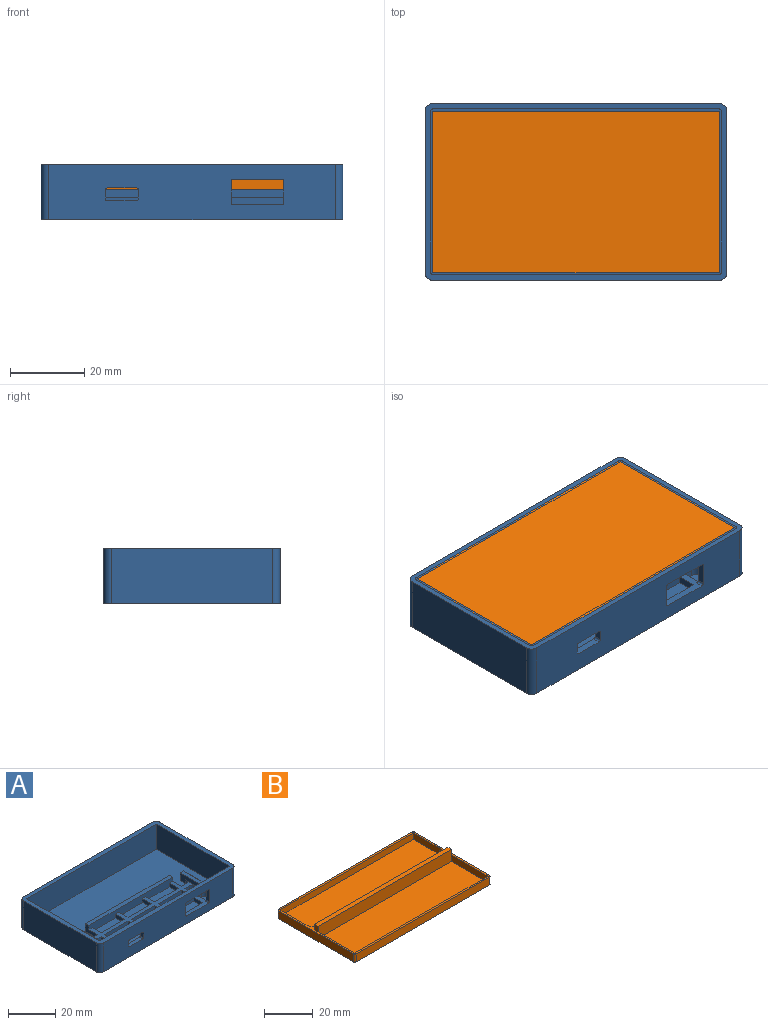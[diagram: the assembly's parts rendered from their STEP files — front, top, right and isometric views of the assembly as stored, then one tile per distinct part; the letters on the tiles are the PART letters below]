
ASSEMBLY  parts=2 mates=1
PART A: 116 faces, bbox 81.4x47.6x15 mm
  f0: plane 5.4x4.6mm, normal (0,0,1), area 24mm2, adj f10,f36,f56,f83,f110
  f1: plane 5.4x4.6mm, normal (0,0,1), area 23.1mm2, adj f36,f53,f55,f80,f85,f112
  f2: plane 50x4mm, normal (0,-1,0), area 184mm2, adj f11,f18,f25,f54,f88,f89,f90,f96
  f3: plane 77.4x43.6mm, normal (0,0,1), area 1884.4mm2, adj f10,f26,f30,f31,f36,f37,f38,f49
  f4: plane 14x2mm, normal (0,1,0), area 28mm2, adj f11,f54,f107,f113
  f5: plane 14x2mm, normal (0,-1,0), area 28mm2, adj f9,f54,f106,f111
  f6: plane 14x2mm, normal (0,1,0), area 28mm2, adj f9,f54,f106,f111
  f7: plane 14x2mm, normal (0,-1,0), area 28mm2, adj f8,f54,f104,f109
  f8: plane 14x5.4mm, normal (0,0,1), area 75.6mm2, adj f7,f10,f104,f109
  f9: plane 14x5.4mm, normal (0,0,1), area 75.6mm2, adj f5,f6,f106,f111
  f10: plane 77.4x13mm, normal (0,1,0), area 722mm2, adj f0,f3,f8,f23,f32,f35,f36,f37
  f11: plane 14x5.4mm, normal (0,0,1), area 75.6mm2, adj f2,f4,f107,f113
  f12: plane 14x2mm, normal (0,1,0), area 28mm2, adj f18,f54,f98,f108
  f13: plane 14x2mm, normal (0,-1,0), area 28mm2, adj f17,f54,f101,f105
  f14: plane 14x2mm, normal (0,1,0), area 28mm2, adj f17,f54,f101,f105
  f15: plane 14x2mm, normal (0,-1,0), area 28mm2, adj f16,f54,f100,f103
  f16: plane 14x5.4mm, normal (0,0,1), area 75.6mm2, adj f15,f33,f100,f103
  f17: plane 14x5.4mm, normal (0,0,1), area 75.6mm2, adj f13,f14,f101,f105
  f18: plane 14x5.4mm, normal (0,0,1), area 75.6mm2, adj f2,f12,f98,f108
  f19: plane 14x2mm, normal (0,1,0), area 28mm2, adj f25,f54,f96,f97
  f20: plane 14x2mm, normal (0,-1,0), area 28mm2, adj f24,f54,f94,f102
  f21: plane 14x2mm, normal (0,1,0), area 28mm2, adj f24,f54,f94,f102
  f22: plane 14x2mm, normal (0,-1,0), area 28mm2, adj f23,f54,f93,f99
  f23: plane 14x5.4mm, normal (0,0,1), area 75.6mm2, adj f10,f22,f93,f99
  f24: plane 14x5.4mm, normal (0,0,1), area 75.6mm2, adj f20,f21,f94,f102
  f25: plane 14x5.4mm, normal (0,0,1), area 75.6mm2, adj f2,f19,f96,f97
  f26: plane 2.6x2mm, normal (0,1,0), area 5.2mm2, adj f3,f54,f87,f90
  f27: plane 2.6x2mm, normal (0,-1,0), area 5.2mm2, adj f39,f54,f86,f95
  f28: plane 2.6x2mm, normal (0,1,0), area 5.2mm2, adj f39,f54,f81,f95
  f29: plane 2.6x2mm, normal (0,-1,0), area 5.2mm2, adj f35,f54,f82,f92
  f30: plane 6x4mm, normal (0,1,0), area 16mm2, adj f3,f50,f51,f115
  f31: plane 6x4mm, normal (0,1,0), area 16mm2, adj f3,f32,f36,f114
  f32: plane 20.2x2mm, normal (0,0,1), area 40.4mm2, adj f10,f31,f36,f114
  f33: plane 14x2mm, normal (0,1,0), area 28mm2, adj f16,f54,f100,f103
  f34: plane 77.4x15mm, normal (0,-1,0), area 1031.9mm2, adj f40,f44,f45,f48,f54,f57,f58,f59
  f35: plane 5.4x4.6mm, normal (0,0,1), area 24mm2, adj f10,f29,f50,f82,f92
  f36: plane 20.2x4mm, normal (-1,0,0), area 56.8mm2, adj f0,f1,f3,f10,f31,f32,f54,f80
  f37: plane 43.6x13mm, normal (-1,0,0), area 566.8mm2, adj f3,f10,f40,f49
  f38: plane 43.6x13mm, normal (1,0,0), area 566.8mm2, adj f3,f10,f40,f49
  f39: plane 5.4x4.6mm, normal (0,0,1), area 23.1mm2, adj f27,f28,f50,f81,f86,f95
  f40: plane 81.4x47.6mm, normal (0,0,1), area 496.6mm2, adj f10,f34,f37,f38,f41,f42,f43,f45
  f41: plane 43.6x15mm, normal (1,0,0), area 654mm2, adj f40,f44,f45,f46
  f42: plane 77.4x15mm, normal (0,1,0), area 1161mm2, adj f40,f44,f46,f47
  f43: plane 43.6x15mm, normal (-1,0,0), area 654mm2, adj f40,f44,f47,f48
  f44: plane 81.4x47.6mm, normal (0,0,-1), area 3871.2mm2, adj f34,f41,f42,f43,f45,f46,f47,f48
  f45: cylinder r=2mm len=15mm, axis (0,0,1), area 47.1mm2, adj f34,f40,f41,f44
  f46: cylinder r=2mm len=15mm, axis (0,0,-1), area 47.1mm2, adj f40,f41,f42,f44
  f47: cylinder r=2mm len=15mm, axis (0,0,1), area 47.1mm2, adj f40,f42,f43,f44
  f48: cylinder r=2mm len=15mm, axis (0,0,-1), area 47.1mm2, adj f34,f40,f43,f44
  f49: plane 77.4x13mm, normal (0,-1,0), area 1006.2mm2, adj f3,f37,f38,f40
  f50: plane 20.2x4mm, normal (1,0,0), area 56.8mm2, adj f3,f10,f30,f35,f39,f51,f54,f81
  f51: plane 20.2x2mm, normal (0,0,1), area 40.4mm2, adj f10,f30,f50,f115
  f52: plane 2.6x2mm, normal (0,1,0), area 5.2mm2, adj f3,f54,f84,f89
  f53: plane 2.6x2mm, normal (0,-1,0), area 5.2mm2, adj f1,f54,f85,f112
  f54: plane 59.2x22.2mm, normal (0,0,1), area 421.1mm2, adj f2,f4,f5,f6,f7,f10,f12,f13
  f55: plane 2.6x2mm, normal (0,1,0), area 5.2mm2, adj f1,f54,f80,f112
  f56: plane 2.6x2mm, normal (0,-1,0), area 5.2mm2, adj f0,f54,f83,f110
  f57: plane 7.8x2mm, normal (0,0,1), area 15.6mm2, adj f10,f34,f64,f66
  f58: plane 2.5x2mm, normal (1,0,0), area 5mm2, adj f10,f34,f64,f65
  f59: plane 7.8x2mm, normal (0,0,-1), area 15.6mm2, adj f10,f34,f65,f67
  f60: plane 2.5x2mm, normal (-1,0,0), area 5mm2, adj f10,f34,f66,f67
  f61: plane 6x2mm, normal (-1,0,0), area 12mm2, adj f10,f34,f68,f70
  f62: plane 6x2mm, normal (1,0,0), area 12mm2, adj f10,f34,f69,f71
  f63: plane 13.1x2mm, normal (0,0,-1), area 26.2mm2, adj f10,f34,f70,f71
  f64: cylinder r=0.5mm len=2mm, axis (0,1,0), area 1.6mm2, adj f10,f34,f57,f58
  f65: cylinder r=0.5mm len=2mm, axis (0,-1,0), area 1.6mm2, adj f10,f34,f58,f59
  f66: cylinder r=0.5mm len=2mm, axis (0,-1,0), area 1.6mm2, adj f10,f34,f57,f60
  f67: cylinder r=0.5mm len=2mm, axis (0,1,0), area 1.6mm2, adj f10,f34,f59,f60
  f68: cylinder r=0.5mm len=2mm, axis (0,1,0), area 1.6mm2, adj f10,f34,f54,f61
  f69: cylinder r=0.5mm len=2mm, axis (0,-1,0), area 1.6mm2, adj f10,f34,f54,f62
  f70: cylinder r=0.5mm len=2mm, axis (0,-1,0), area 1.6mm2, adj f10,f34,f61,f63
  f71: cylinder r=0.5mm len=2mm, axis (0,1,0), area 1.6mm2, adj f10,f34,f62,f63
  f72: plane 18x1.2mm, normal (0,0,-1), area 21.6mm2, adj f10,f73,f78,f79
  f73: cylinder r=1mm len=1.2mm, axis (0,1,0), area 1.9mm2, adj f10,f72,f74,f79
  f74: plane 2x1.2mm, normal (-1,0,0), area 2.4mm2, adj f10,f73,f75,f79
  f75: cylinder r=1mm len=1.2mm, axis (0,1,0), area 1.9mm2, adj f10,f54,f74,f79
  f76: cylinder r=1mm len=1.2mm, axis (0,1,0), area 1.9mm2, adj f10,f54,f77,f79
  f77: plane 2x1.2mm, normal (1,0,0), area 2.4mm2, adj f10,f76,f78,f79
  f78: cylinder r=1mm len=1.2mm, axis (0,1,0), area 1.9mm2, adj f10,f72,f77,f79
  f79: plane 20x4mm, normal (0,1,0), area 79.1mm2, adj f54,f72,f73,f74,f75,f76,f77,f78
  f80: cylinder r=2mm len=2mm, axis (0,0,1), area 6.3mm2, adj f1,f36,f54,f55
  f81: cylinder r=2mm len=2mm, axis (0,0,-1), area 6.3mm2, adj f28,f39,f50,f54
  f82: cylinder r=2mm len=2mm, axis (0,0,1), area 6.3mm2, adj f29,f35,f50,f54
  f83: cylinder r=2mm len=2mm, axis (0,0,-1), area 6.3mm2, adj f0,f36,f54,f56
  f84: cylinder r=2mm len=2mm, axis (0,0,-1), area 6.3mm2, adj f3,f36,f52,f54
  f85: cylinder r=2mm len=2mm, axis (0,0,1), area 6.3mm2, adj f1,f36,f53,f54
  f86: cylinder r=2mm len=2mm, axis (0,0,-1), area 6.3mm2, adj f27,f39,f50,f54
  f87: cylinder r=2mm len=2mm, axis (0,0,1), area 6.3mm2, adj f3,f26,f50,f54
  f88: plane 50x2mm, normal (0,0,1), area 100mm2, adj f2,f89,f90,f91
  f89: plane 7.4x4mm, normal (1,0,0), area 18.8mm2, adj f2,f3,f52,f54,f88,f91
  f90: plane 7.4x4mm, normal (-1,0,0), area 18.8mm2, adj f2,f3,f26,f54,f88,f91
  f91: plane 50x4mm, normal (0,1,0), area 200mm2, adj f3,f88,f89,f90
  f92: plane 5.4x2mm, normal (-1,0,0), area 10.8mm2, adj f10,f29,f35,f54
  f93: plane 5.4x2mm, normal (1,0,0), area 10.8mm2, adj f10,f22,f23,f54
  f94: plane 5.4x2mm, normal (1,0,0), area 10.8mm2, adj f20,f21,f24,f54
  f95: plane 5.4x2mm, normal (-1,0,0), area 10.8mm2, adj f27,f28,f39,f54
  f96: plane 5.4x2mm, normal (1,0,0), area 10.8mm2, adj f2,f19,f25,f54
  f97: plane 5.4x2mm, normal (-1,0,0), area 10.8mm2, adj f2,f19,f25,f54
  f98: plane 5.4x2mm, normal (1,0,0), area 10.8mm2, adj f2,f12,f18,f54
  f99: plane 5.4x2mm, normal (-1,0,0), area 10.8mm2, adj f10,f22,f23,f54
  f100: plane 5.4x2mm, normal (1,0,0), area 10.8mm2, adj f15,f16,f33,f54
  f101: plane 5.4x2mm, normal (1,0,0), area 10.8mm2, adj f13,f14,f17,f54
  f102: plane 5.4x2mm, normal (-1,0,0), area 10.8mm2, adj f20,f21,f24,f54
  f103: plane 5.4x2mm, normal (-1,0,0), area 10.8mm2, adj f15,f16,f33,f54
  f104: plane 5.4x2mm, normal (1,0,0), area 10.8mm2, adj f7,f8,f10,f54
  f105: plane 5.4x2mm, normal (-1,0,0), area 10.8mm2, adj f13,f14,f17,f54
  f106: plane 5.4x2mm, normal (1,0,0), area 10.8mm2, adj f5,f6,f9,f54
  f107: plane 5.4x2mm, normal (1,0,0), area 10.8mm2, adj f2,f4,f11,f54
  f108: plane 5.4x2mm, normal (-1,0,0), area 10.8mm2, adj f2,f12,f18,f54
  f109: plane 5.4x2mm, normal (-1,0,0), area 10.8mm2, adj f7,f8,f10,f54
  f110: plane 5.4x2mm, normal (1,0,0), area 10.8mm2, adj f0,f10,f54,f56
  f111: plane 5.4x2mm, normal (-1,0,0), area 10.8mm2, adj f5,f6,f9,f54
  f112: plane 5.4x2mm, normal (1,0,0), area 10.8mm2, adj f1,f53,f54,f55
  f113: plane 5.4x2mm, normal (-1,0,0), area 10.8mm2, adj f2,f4,f11,f54
  f114: plane 20.2x4mm, normal (0.71,0,0.71), area 114.3mm2, adj f3,f10,f31,f32
  f115: plane 20.2x4mm, normal (-0.71,0,0.71), area 114.3mm2, adj f3,f10,f30,f51
PART B: 25 faces, bbox 78.6x44.8x6.8 mm
  f0: plane 21.2x3.2mm, normal (-1,0,0), area 67.8mm2, adj f3,f13,f17,f21
  f1: plane 21.2x3.2mm, normal (1,0,0), area 67.8mm2, adj f3,f13,f17,f21
  f2: plane 77x20mm, normal (0,0,1), area 1529.3mm2, adj f14,f15,f16,f20,f23,f24
  f3: plane 78.6x44.8mm, normal (0,0,1), area 205.1mm2, adj f0,f1,f4,f5,f6,f7,f9,f10
  f4: plane 77x4mm, normal (0,-1,0), area 308mm2, adj f3,f8,f9,f12
  f5: plane 43.2x4mm, normal (1,0,0), area 172.8mm2, adj f3,f8,f9,f10
  f6: plane 77x4mm, normal (0,1,0), area 308mm2, adj f3,f8,f10,f11
  f7: plane 43.2x4mm, normal (-1,0,0), area 172.8mm2, adj f3,f8,f11,f12
  f8: plane 78.6x44.8mm, normal (0,0,-1), area 3520.7mm2, adj f4,f5,f6,f7,f9,f10,f11,f12
  f9: cylinder r=0.8mm len=4mm, axis (0,0,1), area 5mm2, adj f3,f4,f5,f8
  f10: cylinder r=0.8mm len=4mm, axis (0,0,-1), area 5mm2, adj f3,f5,f6,f8
  f11: cylinder r=0.8mm len=4mm, axis (0,0,1), area 5mm2, adj f3,f6,f7,f8
  f12: cylinder r=0.8mm len=4mm, axis (0,0,-1), area 5mm2, adj f3,f4,f7,f8
  f13: plane 77x3.2mm, normal (0,1,0), area 246.4mm2, adj f0,f1,f3,f17
  f14: plane 15x3.2mm, normal (-1,0,0), area 48mm2, adj f2,f3,f15,f23
  f15: plane 77x3.2mm, normal (0,-1,0), area 246.4mm2, adj f2,f3,f14,f16
  f16: plane 15x3.2mm, normal (1,0,0), area 48mm2, adj f2,f3,f15,f24
  f17: plane 77x21.2mm, normal (0,0,1), area 1632.4mm2, adj f0,f1,f13,f21
  f18: plane 2.8x2mm, normal (1,0,0), area 5.6mm2, adj f3,f20,f21,f22
  f19: plane 2.8x2mm, normal (-1,0,0), area 5.6mm2, adj f3,f20,f21,f22
  f20: plane 77x6mm, normal (0,1,0), area 430mm2, adj f2,f3,f18,f19,f22,f23,f24
  f21: plane 77x6mm, normal (0,-1,0), area 462mm2, adj f0,f1,f17,f18,f19,f22
  f22: plane 77x2mm, normal (0,0,1), area 154mm2, adj f18,f19,f20,f21
  f23: cylinder r=5mm len=5mm, axis (0,0,1), area 25.1mm2, adj f2,f3,f14,f20
  f24: cylinder r=5mm len=5mm, axis (0,0,-1), area 25.1mm2, adj f2,f3,f16,f20
PLACE A at identity
PLACE B rot(axis=(-1,0,0),180deg) t=(0,0,15)mm
MATE fastened A.f40 <-> B.f8  axis (0,0,1) through (0,0,15)mm
